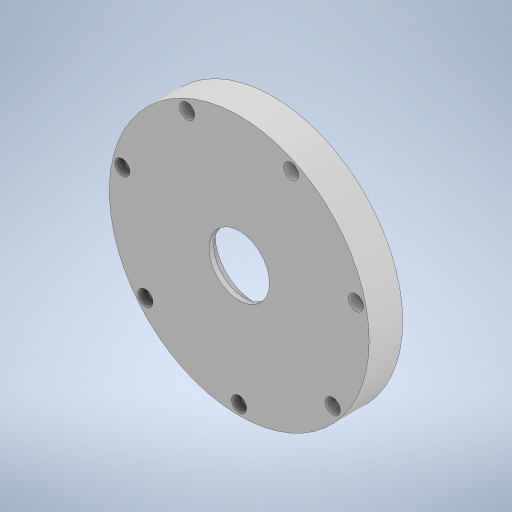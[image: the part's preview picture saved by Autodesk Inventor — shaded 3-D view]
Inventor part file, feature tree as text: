
AUTODESK INVENTOR PART (.ipt)
format: ipt  version: 2023 (Build 270158000, 158)  size: 316,416 bytes
history: native  units: in
note: dims shown in document units (in); Inventor stores cm internally (conversion verified against a paired STEP export)
features: sketch x7, extrude x6, pattern_circular x1
ambient origin geometry x8: Origin, YZ Plane, XZ Plane, XY Plane, X Axis, Y Axis, Z Axis, Center Point
bodies: Solid1 (feature_tree)
feature tree (14):
  extrude  "Extrusion1"  Depth=0.7874in TaperAngle=0.0deg
  extrude  "Extrusion2"  Depth=4.7244in
  extrude  "Extrusion3"  Depth=0.1181in TaperAngle=0.0deg
  extrude  "Extrusion4"  TaperAngle=0.0deg  [1 undecoded]
  pattern_circular  "Circular Pattern1"  [2 undecoded]
  extrude  "Extrusion5"  Depth=0.2441in TaperAngle=360.0deg
  extrude  "Extrusion6"  Depth=0.2441in
  sketch  "Sketch1"  dims[d0=6.1024in d1=0.7874in d2=0.0in]
  sketch  "Sketch2"  dims[d3=0.2362in d4=4.7244in]
  sketch  "Sketch3"  dims[d5=8.2677in d7=360.0deg d9=0.1181in d10=0.0in]
  sketch  "Sketch4"  dims[d11=1.4173in d12=0.0in d13=0.0in]
  sketch  "Sketch5"  dims[d14=3.622in]
  sketch  "Sketch6"  dims[d15=0.4331in d16=0.0in]
  sketch  "Sketch7"  dims[d17=0.2362in d18=0.2362in d19=0.3543in d20=0.2165in d21=90.0deg d22=0.2362in d23=0.0in d24=5.6299in d25=2.7559in d26=360.0deg d28=5.1181in d29=0.0394in d30=0.0in d31=1.8504in d32=0.2441in d33=0.0in]
note: 3 required parameter values undecoded (feature->parameter linkage not recoverable at this tier; creation-order binding heuristic only, values carry confidence <= 0.55)
